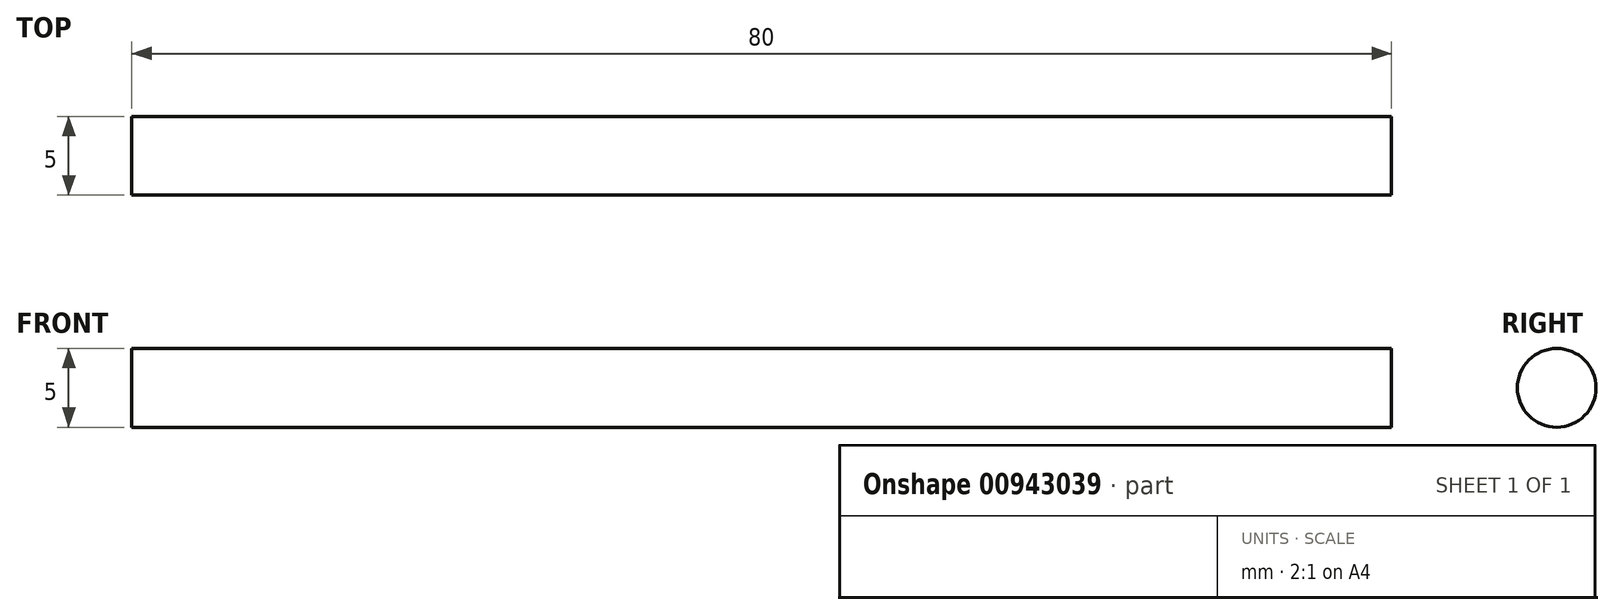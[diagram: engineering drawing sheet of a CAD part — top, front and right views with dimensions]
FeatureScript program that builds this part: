
annotation { "Feature Type Name" : "Feature", "Feature Type Description" : "" }
export const myFeature = defineFeature(function(context is Context, id is Id, definition is map)
    precondition{}
    {
        {
            var Q0;
            Q0=qCreatedBy(makeId("Right.planeOp"),FACE);
            var sketch = newSketch(context, id + "F0", { "sketchPlane" : qUnion([Q0])});
            skCircle(sketch, "E0", {"center": v(0, 0) * mm, "radius": 2.5 * mm});
            skSolve(sketch);
        }
        {
            var Q0;
            Q0=qSketchRegion(id+"F0",true);
            extrude(context, id + "F1", {"entities" : qUnion([Q0]), "depth" : 80 * mm, "offsetDistance" : 25 * mm});
        }
    });
